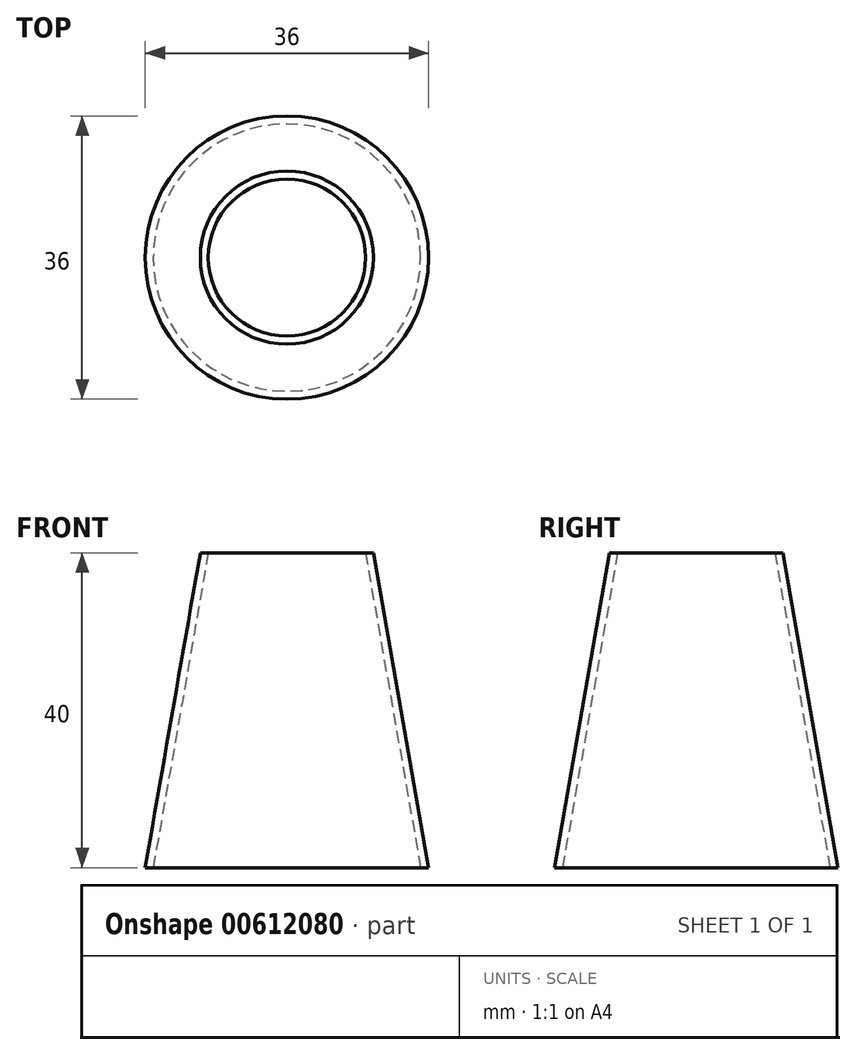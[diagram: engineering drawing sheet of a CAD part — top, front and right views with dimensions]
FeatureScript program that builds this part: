
annotation { "Feature Type Name" : "Feature", "Feature Type Description" : "" }
export const myFeature = defineFeature(function(context is Context, id is Id, definition is map)
    precondition{}
    {
        {
            var Q0;
            Q0=qCreatedBy(makeId("Front.planeOp"),FACE);
            var sketch = newSketch(context, id + "F0", { "sketchPlane" : qUnion([Q0])});
            skLineSegment(sketch, "E0.bottom", {"start": v(0, 0) * mm, "end": v(11, 0) * mm});
            skLineSegment(sketch, "E0.top", {"start": v(0, 40) * mm, "end": v(11, 40) * mm});
            skLineSegment(sketch, "E0.left", {"start": v(0, 0) * mm, "end": v(0, 40) * mm});
            skLineSegment(sketch, "E0.right", {"start": v(11, 0) * mm, "end": v(11, 40) * mm});
            skLineSegment(sketch, "E1.bottom", {"start": v(0, 0) * mm, "end": v(18, 0) * mm});
            skLineSegment(sketch, "E1.top", {"start": v(0, 9.86) * mm, "end": v(18, 9.86) * mm});
            skLineSegment(sketch, "E1.left", {"start": v(0, 0) * mm, "end": v(0, 9.86) * mm});
            skLineSegment(sketch, "E1.right", {"start": v(18, 0) * mm, "end": v(18, 9.86) * mm});
            skLineSegment(sketch, "E2", {"start": v(11, 40) * mm, "end": v(18, 0) * mm});
            skLineSegment(sketch, "E3", {"start": v(9.98, 40) * mm, "end": v(16.98, 0) * mm});
            skSolve(sketch);
        }
        {
            var Q0;
            {var subQ0=sQuery(id+"F0.wireOp",EDGE,"E2");var subQ5=sQuery(id+"F0.wireOp",EDGE,"E1.top");var subQ6=makeQuery(id+"F0.imprint","INTERSECT",VERTEX,{"derivedFrom":[subQ5,subQ0]});Q0=makeQuery(id+"F0.imprint","IMPRINT",FACE,{"disambiguationData":[TD([[makeQuery(id+"F0.imprint","IMPRINT",EDGE,{"disambiguationData":[TD([[subQ6,1.0]])],"derivedFrom":subQ5}),-1.0]])]});}
            var Q1;
            {var subQ0=sQuery(id+"F0.wireOp",EDGE,"E2");var subQ5=sQuery(id+"F0.wireOp",EDGE,"E1.top");var subQ6=makeQuery(id+"F0.imprint","INTERSECT",VERTEX,{"derivedFrom":[subQ5,subQ0]});Q1=makeQuery(id+"F0.imprint","IMPRINT",FACE,{"disambiguationData":[TD([[makeQuery(id+"F0.imprint","IMPRINT",EDGE,{"disambiguationData":[TD([[subQ6,1.0]])],"derivedFrom":subQ5}),1.0]])]});}
            var Q2;
            {var subQ1=sQuery(id+"F0.wireOp",EDGE,"E0.top");var subQ3=sQuery(id+"F0.wireOp",EDGE,"E3");var subQ4=makeQuery(id+"F0.imprint","INTERSECT",VERTEX,{"derivedFrom":[subQ1,subQ3]});Q2=makeQuery(id+"F0.imprint","IMPRINT",FACE,{"disambiguationData":[TD([[makeQuery(id+"F0.imprint","IMPRINT",EDGE,{"disambiguationData":[TD([[subQ4,-1.0]])],"derivedFrom":subQ3}),1.0]])]});}
            var Q3;
            Q3=sQuery(id+"F0.wireOp",EDGE,"E0.left");
            revolve(context, id + "F1", {"entities" : qUnion([Q0, Q1, Q2]), "axis" : qUnion([Q3]), "revolveType" : RevolveType.FULL});
        }
    });
